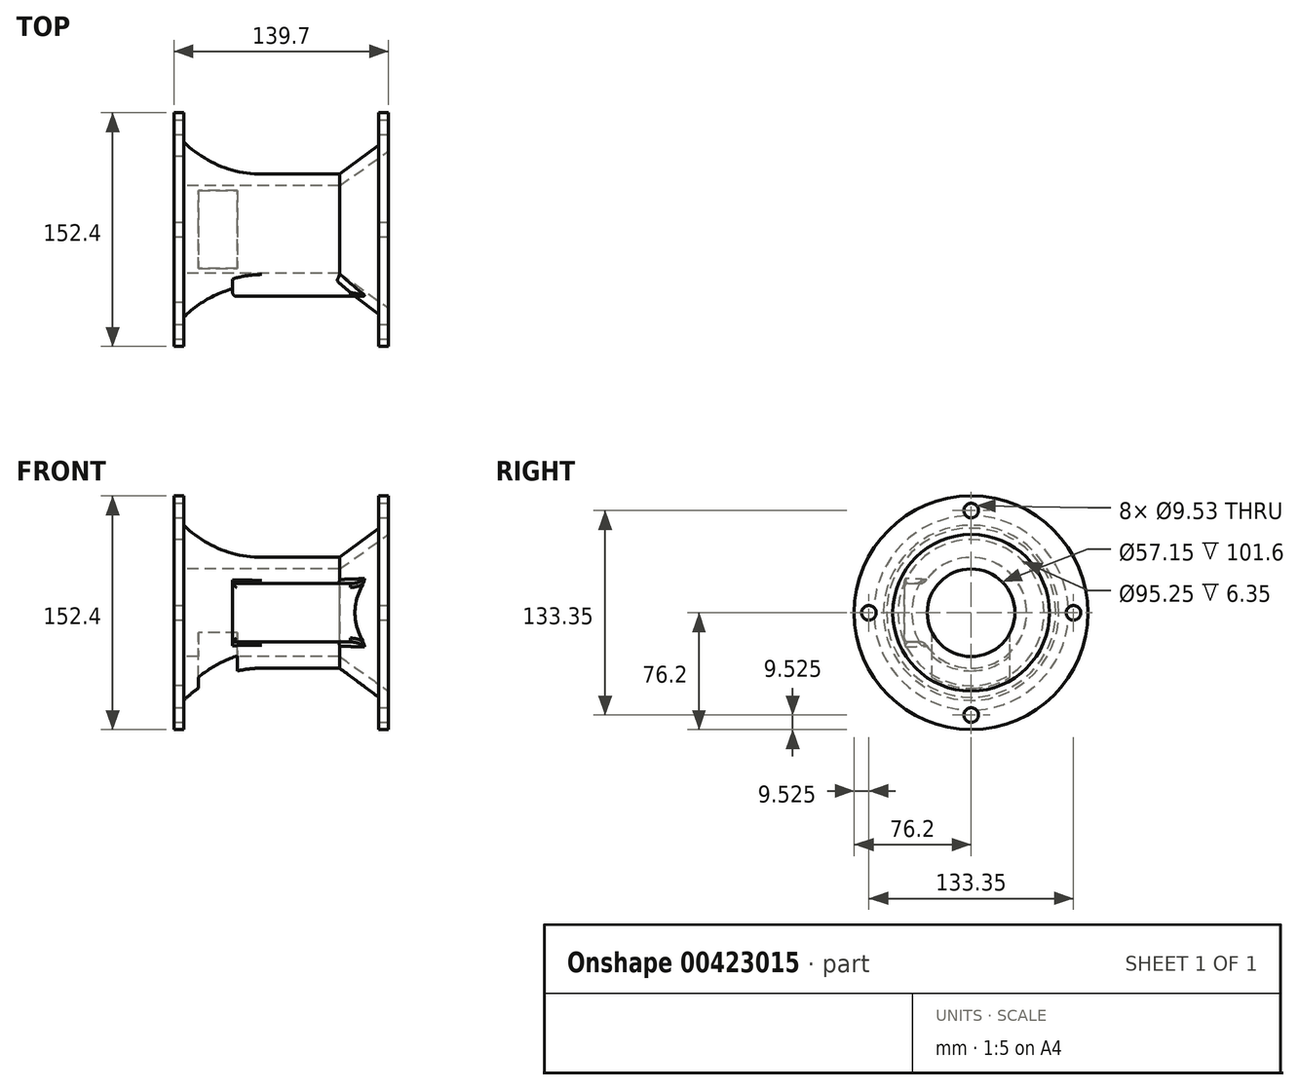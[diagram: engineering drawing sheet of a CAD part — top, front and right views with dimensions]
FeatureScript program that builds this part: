
annotation { "Feature Type Name" : "Feature", "Feature Type Description" : "" }
export const myFeature = defineFeature(function(context is Context, id is Id, definition is map)
    precondition{}
    {
        {
            var Q0;
            Q0=qCreatedBy(makeId("Right.planeOp"),FACE);
            var sketch = newSketch(context, id + "F0", { "sketchPlane" : qUnion([Q0])});
            skCircle(sketch, "E0", {"center": v(0, 0) * mm, "radius": 76.2 * mm});
            skCircle(sketch, "E1", {"center": v(0, 0) * mm, "radius": 47.63 * mm});
            skSolve(sketch);
        }
        {
            var Q0;
            Q0=makeQuery(id+"F0.imprint","IMPRINT",FACE,{"disambiguationData":[TD([[makeQuery(id+"F0.imprint","IMPRINT",EDGE,{"derivedFrom":sQuery(id+"F0.wireOp",EDGE,"E0")}),1.0]])]});
            extrude(context, id + "F1", {"entities" : qUnion([Q0]), "depth" : 6.35 * mm});
        }
        {
            var Q0;
            Q0=makeQuery(id+"F1.opExtrude","CAP_FACE",FACE,{"disambiguationData":[OSD([sQuery(id+"F0.wireOp",EDGE,"E0"),sQuery(id+"F0.wireOp",EDGE,"E1")])],"isStart":false});
            var sketch = newSketch(context, id + "F2", { "sketchPlane" : qUnion([Q0])});
            skCircle(sketch, "E2", {"center": v(0, 0) * mm, "radius": 57.15 * mm});
            skSolve(sketch);
        }
        {
            var Q0;
            Q0=makeQuery(id+"F2.imprint","IMPRINT",FACE,{"disambiguationData":[TD([[makeQuery(id+"F2.imprint","IMPRINT",EDGE,{"derivedFrom":sQuery(id+"F2.wireOp",EDGE,"E2")}),1.0]])]});
            var Q1;
            Q1=makeQuery(id+"F2.imprint","IMPRINT",FACE,{"disambiguationData":[TD([[makeQuery(id+"F2.imprint","IMPRINT",EDGE,{"derivedFrom":makeQuery(id+"F1.opExtrude","CAP_EDGE",EDGE,{"disambiguationData":[OSD([sQuery(id+"F0.wireOp",EDGE,"E1")])],"isStart":false})}),1.0]])]});
            extrude(context, id + "F3", {"entities" : qUnion([Q0, Q1]), "operationType" : NewBodyOperationType.ADD, "depth" : 127 * mm});
        }
        {
            var Q0;
            Q0=makeQuery(id+"F3.opExtrude","CAP_FACE",FACE,{"disambiguationData":[OSD([sQuery(id+"F2.wireOp",EDGE,"E2")])],"isStart":false});
            var sketch = newSketch(context, id + "F4", { "sketchPlane" : qUnion([Q0])});
            skCircle(sketch, "E3", {"center": v(0, 0) * mm, "radius": 76.2 * mm});
            skSolve(sketch);
        }
        {
            var Q0;
            Q0=qSketchRegion(id+"F4",true);
            extrude(context, id + "F5", {"entities" : qUnion([Q0]), "operationType" : NewBodyOperationType.ADD, "depth" : 6.35 * mm});
        }
        {
            var Q0;
            Q0=makeQuery(id+"F3.opExtrude","CAP_FACE",FACE,{"disambiguationData":[OSD([sQuery(id+"F2.wireOp",EDGE,"E2")])],"isStart":true});
            var sketch = newSketch(context, id + "F6", { "sketchPlane" : qUnion([Q0])});
            skCircle(sketch, "E4", {"center": v(0, 0) * mm, "radius": 28.58 * mm});
            skSolve(sketch);
        }
        {
            var Q0;
            Q0=makeQuery(id+"F6.imprint","IMPRINT",FACE,{"disambiguationData":[TD([[makeQuery(id+"F6.imprint","IMPRINT",EDGE,{"derivedFrom":sQuery(id+"F6.wireOp",EDGE,"E4")}),1.0]])]});
            extrude(context, id + "F7", {"entities" : qUnion([Q0]), "operationType" : NewBodyOperationType.REMOVE, "oppositeDirection" : true, "depth" : 101.6 * mm});
        }
        {
            var Q0;
            Q0=makeQuery(id+"F7.boolean.opBoolean","COPY",FACE,{"derivedFrom":makeQuery(id+"F7.opExtrude","CAP_FACE",FACE,{"disambiguationData":[OSD([sQuery(id+"F6.wireOp",EDGE,"E4")])],"isStart":false})});
            var sketch = newSketch(context, id + "F8", { "sketchPlane" : qUnion([Q0])});
            skCircle(sketch, "E5", {"center": v(0, 0) * mm, "radius": 28.58 * mm});
            skSolve(sketch);
        }
        {
            var Q0;
            Q0=qSketchRegion(id+"F8",true);
            extrude(context, id + "F9", {"entities" : qUnion([Q0]), "operationType" : NewBodyOperationType.REMOVE, "oppositeDirection" : true, "depth" : 53.97 * mm, "hasDraft" : true, "draftAngle" : 19.65 * degree});
        }
        {
            var Q0;
            Q0=qCreatedBy(makeId("Top.planeOp"),FACE);
            var sketch = newSketch(context, id + "F10", { "sketchPlane" : qUnion([Q0])});
            skLineSegment(sketch, "E6.bottom", {"start": v(41.27, 25.4) * mm, "end": v(15.88, 25.4) * mm});
            skLineSegment(sketch, "E6.top", {"start": v(41.27, -25.4) * mm, "end": v(15.87, -25.4) * mm});
            skLineSegment(sketch, "E6.left", {"start": v(41.27, 25.4) * mm, "end": v(41.27, -25.4) * mm});
            skLineSegment(sketch, "E6.right", {"start": v(15.88, 25.4) * mm, "end": v(15.87, -25.4) * mm});
            skPoint(sketch, "E6.middle", {"position": v(28.57, 0) * mm});
            skSolve(sketch);
        }
        {
            var Q0;
            Q0=qSketchRegion(id+"F10",true);
            extrude(context, id + "F11", {"entities" : qUnion([Q0]), "operationType" : NewBodyOperationType.REMOVE, "oppositeDirection" : true, "depth" : 76.2 * mm});
        }
        {
            var Q0;
            Q0=qCreatedBy(makeId("Top.planeOp"),FACE);
            var sketch = newSketch(context, id + "F12", { "sketchPlane" : qUnion([Q0])});
            skLineSegment(sketch, "E7.bottom", {"start": v(18.63, 39.07) * mm, "end": v(6.35, 39.07) * mm});
            skLineSegment(sketch, "E7.top", {"start": v(18.63, -39.07) * mm, "end": v(6.35, -39.07) * mm});
            skLineSegment(sketch, "E7.left", {"start": v(18.63, 39.07) * mm, "end": v(18.63, -39.07) * mm});
            skLineSegment(sketch, "E7.right", {"start": v(6.35, 39.07) * mm, "end": v(6.35, -39.07) * mm});
            skPoint(sketch, "E7.middle", {"position": v(12.5, 0) * mm});
            skSolve(sketch);
        }
        {
            var Q0;
            Q0=qCreatedBy(makeId("Front.planeOp"),FACE);
            var sketch = newSketch(context, id + "F13", { "sketchPlane" : qUnion([Q0])});
            skLineSegment(sketch, "E8", {"start": v(0, 0) * mm, "end": v(154.85, 0) * mm});
            skSolve(sketch);
        }
        {
            var Q0;
            Q0=qCreatedBy(makeId("Front.planeOp"),FACE);
            var sketch = newSketch(context, id + "F14", { "sketchPlane" : qUnion([Q0])});
            skLineSegment(sketch, "E9", {"start": v(133.35, 55.13) * mm, "end": v(107.95, 36.15) * mm});
            skLineSegment(sketch, "E10", {"start": v(107.95, 36.15) * mm, "end": v(57.15, 36.15) * mm});
            skArc(sketch, "E11", {"start": v(57.15, 36.15) * mm, "mid": v(29.66, 41.6) * mm, "end": v(6.35, 57.16) * mm});
            skLineSegment(sketch, "E12", {"start": v(6.35, 57.16) * mm, "end": v(6.35, 63.39) * mm});
            skLineSegment(sketch, "E13", {"start": v(6.35, 63.39) * mm, "end": v(133.75, 63.39) * mm});
            skLineSegment(sketch, "E14", {"start": v(133.75, 63.39) * mm, "end": v(133.35, 55.13) * mm});
            skSolve(sketch);
        }
        {
            var Q0;
            Q0=qCreatedBy(makeId("Front.planeOp"),FACE);
            cPlane(context, id + "F15", {"entities" : qUnion([Q0]), "cplaneType" : CPlaneType.OFFSET, "offset" : 28.57 * mm, "width" : 152.4 * mm, "height" : 152.4 * mm});
        }
        {
            var Q0;
            Q0=qSketchRegion(id+"F14",true);
            var Q1;
            Q1=sQuery(id+"F13.wireOp",EDGE,"E8");
            revolve(context, id + "F16", {"operationType" : NewBodyOperationType.REMOVE, "entities" : qUnion([Q0]), "axis" : qUnion([Q1]), "revolveType" : RevolveType.FULL, "oppositeDirection" : true});
        }
        {
            var Q0;
            Q0=qCreatedBy(id+"F15.planeOp",FACE);
            var sketch = newSketch(context, id + "F17", { "sketchPlane" : qUnion([Q0])});
            skLineSegment(sketch, "E15.bottom", {"start": v(127, 19.05) * mm, "end": v(38.1, 19.05) * mm});
            skLineSegment(sketch, "E15.top", {"start": v(127, -19.05) * mm, "end": v(38.1, -19.05) * mm});
            skLineSegment(sketch, "E15.left", {"start": v(127, 19.05) * mm, "end": v(127, -19.05) * mm});
            skLineSegment(sketch, "E15.right", {"start": v(38.1, 19.05) * mm, "end": v(38.1, -19.05) * mm});
            skPoint(sketch, "E15.middle", {"position": v(82.55, 0) * mm});
            skSolve(sketch);
        }
        {
            var Q0;
            Q0=qSketchRegion(id+"F17",true);
            extrude(context, id + "F18", {"entities" : qUnion([Q0]), "operationType" : NewBodyOperationType.ADD, "depth" : 15 * mm});
        }
        {
            var Q0;
            Q0=makeQuery(id+"F18.boolean.opBoolean","INTERSECT",EDGE,{"derivedFrom":[makeQuery(id+"F16.boolean.opBoolean","COPY",FACE,{"derivedFrom":makeQuery(id+"F16.opRevolve","SWEPT_FACE",FACE,{"disambiguationData":[OSD([sQuery(id+"F14.wireOp",EDGE,"E9")])]})}),makeQuery(id+"F18.opExtrude","SWEPT_FACE",FACE,{"disambiguationData":[OSD([sQuery(id+"F17.wireOp",EDGE,"E15.bottom")])]})]});
            var Q1;
            Q1=makeQuery(id+"F18.boolean.opBoolean","INTERSECT",EDGE,{"derivedFrom":[makeQuery(id+"F16.boolean.opBoolean","COPY",FACE,{"derivedFrom":makeQuery(id+"F16.opRevolve","SWEPT_FACE",FACE,{"disambiguationData":[OSD([sQuery(id+"F14.wireOp",EDGE,"E10")])]})}),makeQuery(id+"F18.opExtrude","SWEPT_FACE",FACE,{"disambiguationData":[OSD([sQuery(id+"F17.wireOp",EDGE,"E15.bottom")])]})]});
            var Q2;
            Q2=makeQuery(id+"F18.boolean.opBoolean","INTERSECT",EDGE,{"derivedFrom":[makeQuery(id+"F16.boolean.opBoolean","COPY",FACE,{"derivedFrom":makeQuery(id+"F16.opRevolve","SWEPT_FACE",FACE,{"disambiguationData":[OSD([sQuery(id+"F14.wireOp",EDGE,"E10")])]})}),makeQuery(id+"F18.opExtrude","SWEPT_FACE",FACE,{"disambiguationData":[OSD([sQuery(id+"F17.wireOp",EDGE,"E15.top")])]})]});
            var Q3;
            Q3=makeQuery(id+"F18.boolean.opBoolean","INTERSECT",EDGE,{"derivedFrom":[makeQuery(id+"F16.boolean.opBoolean","COPY",FACE,{"derivedFrom":makeQuery(id+"F16.opRevolve","SWEPT_FACE",FACE,{"disambiguationData":[OSD([sQuery(id+"F14.wireOp",EDGE,"E9")])]})}),makeQuery(id+"F18.opExtrude","SWEPT_FACE",FACE,{"disambiguationData":[OSD([sQuery(id+"F17.wireOp",EDGE,"E15.top")])]})]});
            var Q4;
            Q4=makeQuery(id+"F18.boolean.opBoolean","INTERSECT",EDGE,{"derivedFrom":[makeQuery(id+"F16.boolean.opBoolean","COPY",FACE,{"derivedFrom":makeQuery(id+"F16.opRevolve","SWEPT_FACE",FACE,{"disambiguationData":[OSD([sQuery(id+"F14.wireOp",EDGE,"E10")])]})}),makeQuery(id+"F18.opExtrude","SWEPT_FACE",FACE,{"disambiguationData":[OSD([sQuery(id+"F17.wireOp",EDGE,"E15.right")])]})]});
            fillet(context, id + "F19", {"entities" : qUnion([Q0, Q1, Q2, Q3, Q4]), "radius" : 5.08 * mm, "tangentPropagation" : true, "allowEdgeOverflow" : false});
        }
        {
            var Q0;
            Q0=qCreatedBy(makeId("Top.planeOp"),FACE);
            var sketch = newSketch(context, id + "F20", { "sketchPlane" : qUnion([Q0])});
            skLineSegment(sketch, "E16", {"start": v(107.95, 28.58) * mm, "end": v(140.17, 51.4) * mm});
            skLineSegment(sketch, "E17", {"start": v(107.95, 28.58) * mm, "end": v(107.95, 0) * mm});
            skLineSegment(sketch, "E18", {"start": v(140.17, 51.4) * mm, "end": v(140.17, 0) * mm});
            skLineSegment(sketch, "E19", {"start": v(140.17, 0) * mm, "end": v(107.95, 0) * mm});
            skSolve(sketch);
        }
        {
            var Q0;
            Q0=qCreatedBy(makeId("Top.planeOp"),FACE);
            var sketch = newSketch(context, id + "F21", { "sketchPlane" : qUnion([Q0])});
            skLineSegment(sketch, "E20", {"start": v(-10.63, 0) * mm, "end": v(161.7, 0) * mm});
            skSolve(sketch);
        }
        {
            var Q0;
            Q0=qSketchRegion(id+"F20",true);
            var Q1;
            Q1=sQuery(id+"F21.wireOp",EDGE,"E20");
            revolve(context, id + "F22", {"operationType" : NewBodyOperationType.REMOVE, "entities" : qUnion([Q0]), "axis" : qUnion([Q1]), "revolveType" : RevolveType.FULL, "oppositeDirection" : true});
        }
        {
            var Q0;
            Q0=makeQuery(id+"F18.opExtrude","CAP_EDGE",EDGE,{"disambiguationData":[OSD([sQuery(id+"F17.wireOp",EDGE,"E15.top")])],"isStart":false});
            var Q1;
            Q1=makeQuery(id+"F18.opExtrude","CAP_EDGE",EDGE,{"disambiguationData":[OSD([sQuery(id+"F17.wireOp",EDGE,"E15.right")])],"isStart":false});
            var Q2;
            Q2=makeQuery(id+"F18.opExtrude","CAP_EDGE",EDGE,{"disambiguationData":[OSD([sQuery(id+"F17.wireOp",EDGE,"E15.bottom")])],"isStart":false});
            fillet(context, id + "F23", {"entities" : qUnion([Q0, Q1, Q2]), "radius" : 2.54 * mm, "tangentPropagation" : true, "allowEdgeOverflow" : false});
        }
        {
            var Q0;
            Q0=makeQuery(id+"F5.opExtrude","CAP_FACE",FACE,{"disambiguationData":[OSD([sQuery(id+"F4.wireOp",EDGE,"E3")])],"isStart":false});
            var sketch = newSketch(context, id + "F24", { "sketchPlane" : qUnion([Q0])});
            skPoint(sketch, "E21", {"position": v(0, 66.67) * mm});
            skPoint(sketch, "E22", {"position": v(66.68, 0) * mm});
            skPoint(sketch, "E23", {"position": v(0, -66.68) * mm});
            skPoint(sketch, "E24", {"position": v(-66.68, 0) * mm});
            skSolve(sketch);
        }
        {
            var Q0;
            Q0=sQuery(id+"F24.wireOp",VERTEX,"E24");
            var Q1;
            Q1=sQuery(id+"F24.wireOp",VERTEX,"E21");
            var Q2;
            Q2=sQuery(id+"F24.wireOp",VERTEX,"E22");
            var Q3;
            Q3=sQuery(id+"F24.wireOp",VERTEX,"E23");
            var Q4;
            Q4=makeQuery(id+"F1.opExtrude","SWEPT_BODY",BODY,{"disambiguationData":[OSD([sQuery(id+"F0.wireOp",EDGE,"E0"),sQuery(id+"F0.wireOp",EDGE,"E1")])]});
            hole(context, id + "F25", {"style" : HoleStyle.C_BORE, "endStyle" : HoleEndStyle.THROUGH, "holeDiameter" : 9.52 * mm, "cBoreDiameter" : 9.52 * mm, "cBoreDepth" : 6.35 * mm, "isTappedThrough" : true, "tappedDepth" : 12.7 * mm, "tapClearance" : 3, "locations" : qUnion([Q0, Q1, Q2, Q3]), "scope" : qUnion([Q4])});
        }
    });
